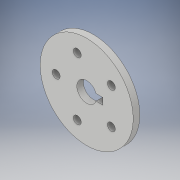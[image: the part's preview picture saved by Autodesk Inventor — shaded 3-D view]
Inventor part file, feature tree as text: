
AUTODESK INVENTOR PART (.ipt)
format: ipt  version: 2017 (Build 210142000, 142)  size: 174,592 bytes
history: native  units: in
note: dims shown in document units (in); Inventor stores cm internally (conversion verified against a paired STEP export)
features: sketch x5, extrude x2, hole x1
ambient origin geometry x8: Origin, YZ Plane, XZ Plane, XY Plane, X Axis, Y Axis, Z Axis, Center Point
bodies: Solid1 (feature_tree)
feature tree (8):
  extrude  "Extrusion1"  Depth=9.4488in TaperAngle=360.0deg
  hole  "Hole1"  [1 undecoded]
  sketch  "Sketch3"  dims[d13=1.9685in d15=360.0deg d17=0.68in]
  sketch  "Sketch4"  dims[d19=0.0in]
  extrude  "Extrusion2"  Depth=0.68in
  sketch  "Sketch1"  dims[d0=3.525in d2=9.4488in d4=360.0deg]
  sketch  "Sketch2"  dims[d6=9.4488in d8=360.0deg d10=0.25in d11=0.0in]
  sketch  "Sketch5"  dims[d20=0.3in d21=0.3in d22=0.75in d23=0.375in d24=0.25in d25=0.5635in d26=1.0in d27=0.8108in d28=0.75in d36=3.525in d40=0.0in d41=0.25in d42=0.125in d43=0.0in d44=0.0in d45=0.0in d46=0.6153in]
note: 1 required parameter value undecoded (feature->parameter linkage not recoverable at this tier; creation-order binding heuristic only, values carry confidence <= 0.55)
